# Revit family: CRTA1X4
name_source: partatom
category: Lighting Fixtures
units: mm (PartAtom-declared; Revit-internal decimal feet)

## family parameters
Always vertical = Yes
Cut with Voids When Loaded = No
Host = Ceiling
Light Source = Yes
Maintain Annotation Orientation = No
OmniClass Number = 23.80.70.11
OmniClass Title = Luminaries for Internal Lighting
Part Type = Normal
Room Calculation Point = No
Round Connector Dimension = Use Diameter
Shared = No

## types (6) — shared parameters
Color Filter = 16777215
Default Elevation = 0' - 0"
Description = LED Recessed Cleanroom Top Access Walkable with Overlapping Door Frame
Dimming Lamp Color Temperature Shift = <None>
Emit Shape Visible in Rendering = No
Emit from Rectangle Length = 1' - 3 3/32"
Emit from Rectangle Width = 4' - 3 3/32"
Housing Finish = <By Category>
Lamp = LED
Length = 4' - 3 3/32"
Lens Finish = <By Category>
Manufacturer = Certolux
Model = CRTA
Tilt Angle = 90.00°
URL = https://www.viscor.com
Voltage = 120 V
Width = 1' - 3 3/32"

## per-type parameters (varying)
| type | Apparent Load | Lamp Wattage | Photometric Web File |
| CRTA1X4-LED840K035LUNV-xT-DSA | 25 VA | 25 VA | CRTA-1X4-LED840K035LUNV-xT-DSA.ies |
| CRTA1X4-LED840K055LUNV-xT-DSA | 40 VA | 40 VA | CRTA-1X4-LED840K055LUNV-xT-DSA.ies |
| CRTA1X4-LED840K070LUNV-xT-DSA | 51 VA | 51 VA | CRTA-1X4-LED840K070LUNV-xT-DSA.ies |
| CRTA1X4-LED840K080LUNV-xT-DSA | 59 VA | 59 VA | CRTA-1X4-LED840K080LUNV-xT-DSA.ies |
| CRTA1X4-LED840K100LUNV-xT-DSA | 75 VA | 75 VA | CRTA-1X4-LED840K100LUNV-xT-DSA.ies |
| CRTA1X4-LED840K120LUNV-xT-DSA | 92 VA | 92 VA | CRTA-1X4-LED840K120LUNV-xT-DSA.ies |

## geometry (parser evidence)
native form markers: Sweep x3
no freeform markers — native parametric forms only
